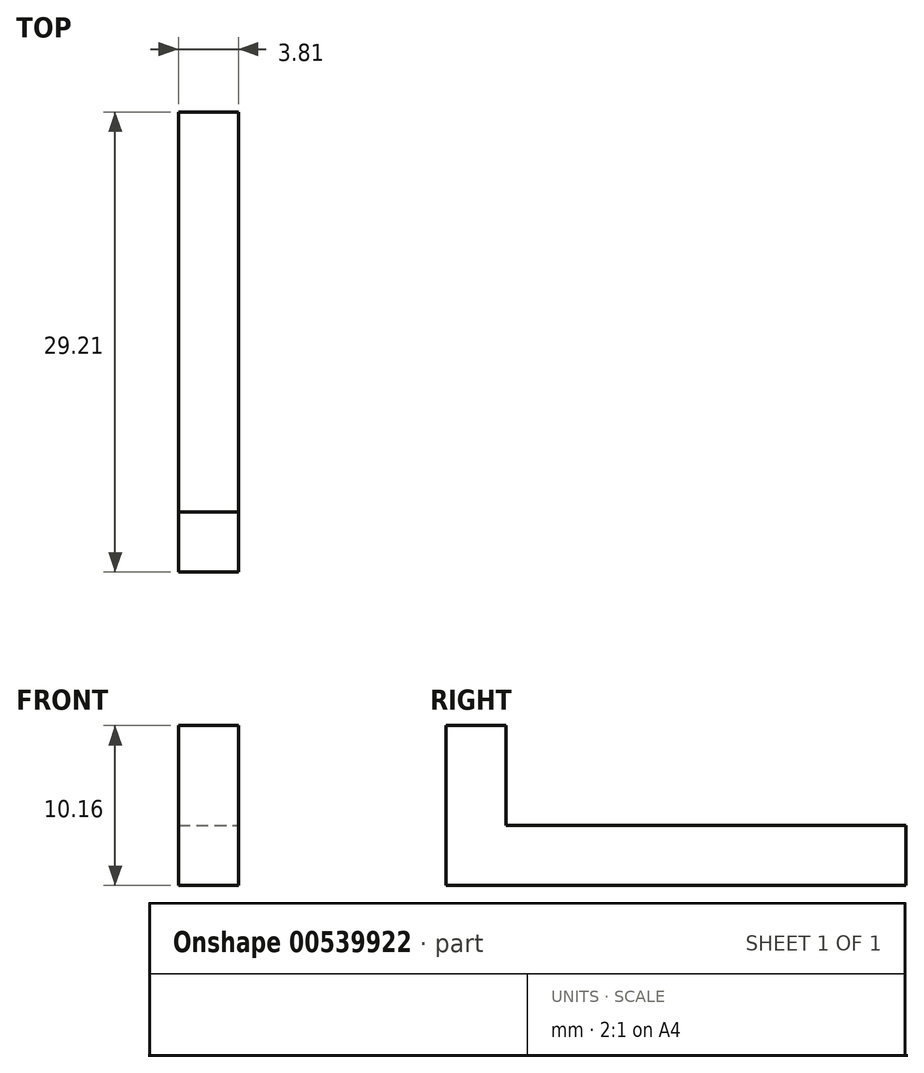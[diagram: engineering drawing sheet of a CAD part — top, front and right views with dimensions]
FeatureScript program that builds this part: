
annotation { "Feature Type Name" : "Feature", "Feature Type Description" : "" }
export const myFeature = defineFeature(function(context is Context, id is Id, definition is map)
    precondition{}
    {
        {
            var Q0;
            Q0=qCreatedBy(makeId("Top.planeOp"),FACE);
            var sketch = newSketch(context, id + "F0", { "sketchPlane" : qUnion([Q0])});
            skLineSegment(sketch, "E0.bottom", {"start": v(0, 0) * mm, "end": v(3.81, 0) * mm});
            skLineSegment(sketch, "E0.top", {"start": v(0, -3.8) * mm, "end": v(3.81, -3.8) * mm});
            skLineSegment(sketch, "E0.left", {"start": v(0, 0) * mm, "end": v(0, -3.8) * mm});
            skLineSegment(sketch, "E0.right", {"start": v(3.81, 0) * mm, "end": v(3.81, -3.8) * mm});
            skSolve(sketch);
        }
        {
            var Q0;
            Q0=makeQuery(id+"F0.imprint","IMPRINT",FACE,{"disambiguationData":[TD([[makeQuery(id+"F0.imprint","IMPRINT",EDGE,{"derivedFrom":sQuery(id+"F0.wireOp",EDGE,"E0.bottom")}),-1.0]])]});
            extrude(context, id + "F1", {"entities" : qUnion([Q0]), "depth" : 10.16 * mm, "offsetDistance" : 25.4 * mm});
        }
        {
            var Q0;
            Q0=makeQuery(id+"F1.opExtrude","SWEPT_FACE",FACE,{"disambiguationData":[OSD([sQuery(id+"F0.wireOp",EDGE,"E0.bottom")])]});
            cPlane(context, id + "F2", {"entities" : qUnion([Q0]), "cplaneType" : CPlaneType.OFFSET, "offset" : 0 * mm, "width" : 152.4 * mm, "height" : 152.4 * mm});
        }
        {
            var Q0;
            Q0=qCreatedBy(id+"F2.planeOp",FACE);
            var sketch = newSketch(context, id + "F3", { "sketchPlane" : qUnion([Q0])});
            skLineSegment(sketch, "E1.bottom", {"start": v(0, 0) * mm, "end": v(-3.81, 0) * mm});
            skLineSegment(sketch, "E1.top", {"start": v(0, 3.81) * mm, "end": v(-3.81, 3.8) * mm});
            skLineSegment(sketch, "E1.left", {"start": v(0, 0) * mm, "end": v(0, 3.81) * mm});
            skLineSegment(sketch, "E1.right", {"start": v(-3.81, 0) * mm, "end": v(-3.81, 3.8) * mm});
            skSolve(sketch);
        }
        {
            var Q0;
            Q0=makeQuery(id+"F3.imprint","IMPRINT",FACE,{"disambiguationData":[TD([[makeQuery(id+"F3.imprint","IMPRINT",EDGE,{"derivedFrom":sQuery(id+"F3.wireOp",EDGE,"E1.bottom")}),-1.0]])]});
            extrude(context, id + "F4", {"entities" : qUnion([Q0]), "operationType" : NewBodyOperationType.ADD, "depth" : 25.4 * mm, "offsetDistance" : 25.4 * mm});
        }
    });
